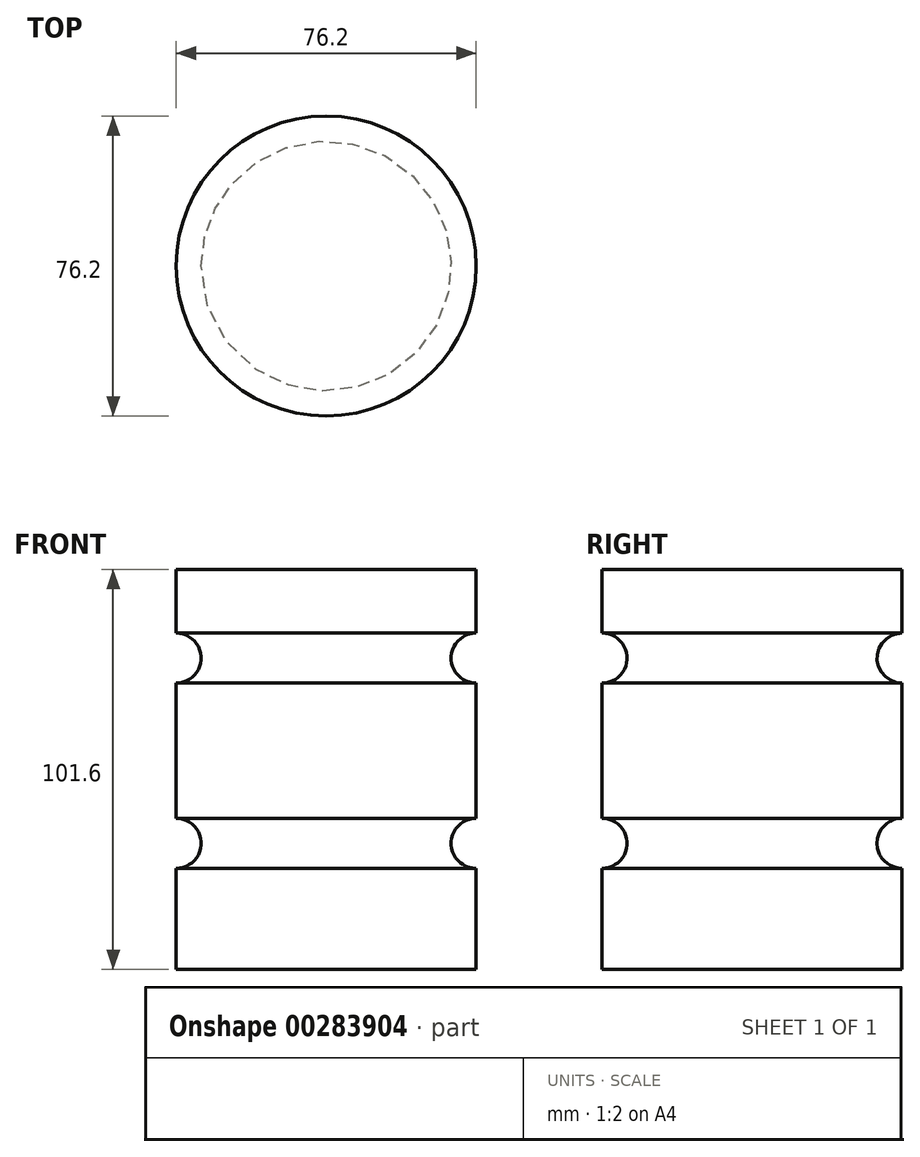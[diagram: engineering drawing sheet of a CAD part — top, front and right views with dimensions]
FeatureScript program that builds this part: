
annotation { "Feature Type Name" : "Feature", "Feature Type Description" : "" }
export const myFeature = defineFeature(function(context is Context, id is Id, definition is map)
    precondition{}
    {
        {
            var Q0;
            Q0=qCreatedBy(makeId("Front.planeOp"),FACE);
            var sketch = newSketch(context, id + "F0", { "sketchPlane" : qUnion([Q0])});
            skLineSegment(sketch, "E0.bottom", {"start": v(0, 0) * mm, "end": v(-38.1, 0) * mm});
            skLineSegment(sketch, "E0.top", {"start": v(0, 101.6) * mm, "end": v(-38.1, 101.6) * mm});
            skLineSegment(sketch, "E0.left", {"start": v(0, 0) * mm, "end": v(0, 101.6) * mm});
            skLineSegment(sketch, "E0.right", {"start": v(-38.1, 0) * mm, "end": v(-38.1, 25.7) * mm});
            skArc(sketch, "E1", {"start": v(-38.1, 25.7) * mm, "mid": v(-31.75, 32.04) * mm, "end": v(-38.1, 38.4) * mm});
            skArc(sketch, "E2", {"start": v(-38.1, 72.74) * mm, "mid": v(-31.75, 79.09) * mm, "end": v(-38.1, 85.44) * mm});
            skLineSegment(sketch, "E3.trimOffspring", {"start": v(-38.1, 38.4) * mm, "end": v(-38.1, 72.74) * mm});
            skLineSegment(sketch, "E4.trimOffspring", {"start": v(-38.1, 85.44) * mm, "end": v(-38.1, 101.6) * mm});
            skSolve(sketch);
        }
        {
            var Q0;
            Q0 = qSketchRegion(id + "F0", true);
            var Q1;
            Q1=sQuery(id+"F0.wireOp",EDGE,"E0.left");
            revolve(context, id + "F1", {"entities" : qUnion([Q0]), "axis" : qUnion([Q1]), "revolveType" : RevolveType.FULL});
        }
    });
